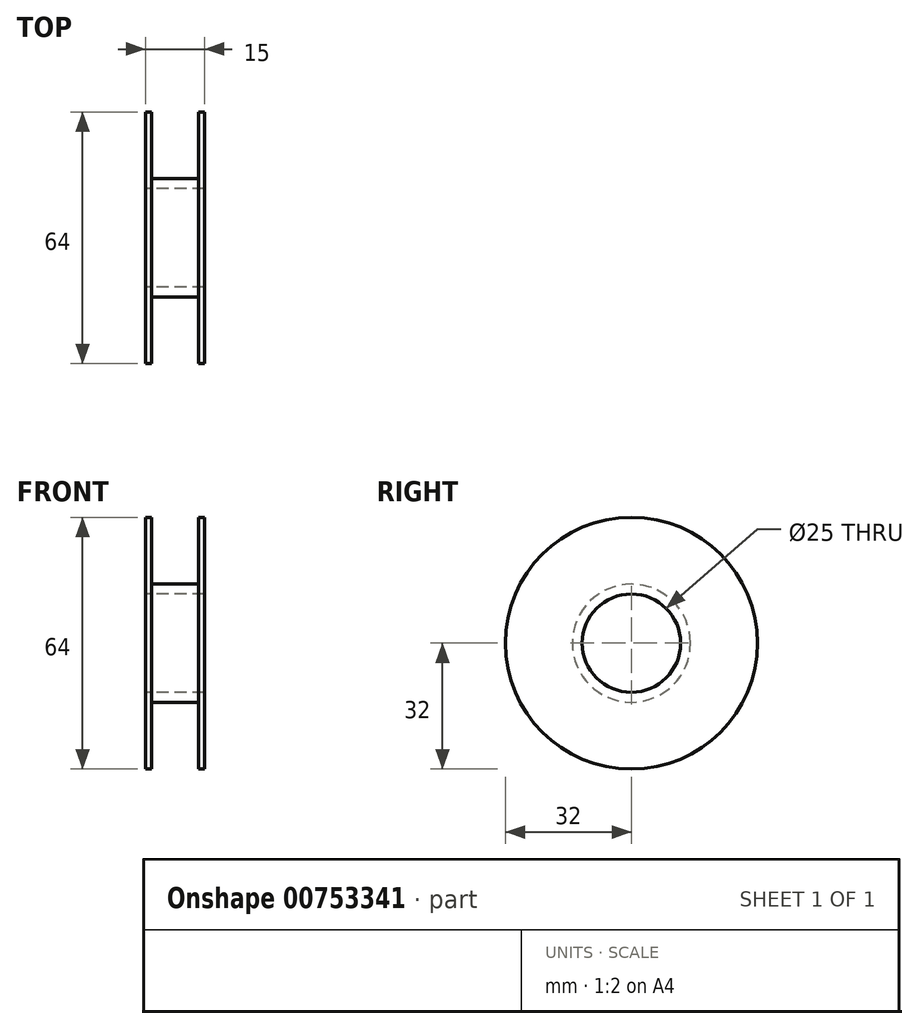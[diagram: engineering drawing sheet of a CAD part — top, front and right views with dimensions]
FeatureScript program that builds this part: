
annotation { "Feature Type Name" : "Feature", "Feature Type Description" : "" }
export const myFeature = defineFeature(function(context is Context, id is Id, definition is map)
    precondition{}
    {
        {
            var Q0;
            Q0=qCreatedBy(makeId("Front.planeOp"),FACE);
            var sketch = newSketch(context, id + "F0", { "sketchPlane" : qUnion([Q0])});
            skLineSegment(sketch, "E0", {"start": v(-7.5, 12.5) * mm, "end": v(-7.5, 32) * mm});
            skLineSegment(sketch, "E1", {"start": v(-7.5, 32) * mm, "end": v(-6, 32) * mm});
            skLineSegment(sketch, "E2", {"start": v(-6, 32) * mm, "end": v(-6, 15) * mm});
            skLineSegment(sketch, "E3", {"start": v(-6, 15) * mm, "end": v(6, 15) * mm});
            skLineSegment(sketch, "E4", {"start": v(6, 15) * mm, "end": v(6, 32) * mm});
            skLineSegment(sketch, "E5", {"start": v(6, 32) * mm, "end": v(7.5, 32) * mm});
            skLineSegment(sketch, "E6", {"start": v(7.5, 32) * mm, "end": v(7.5, 12.5) * mm});
            skLineSegment(sketch, "E7", {"start": v(7.5, 12.5) * mm, "end": v(-7.5, 12.5) * mm});
            skLineSegment(sketch, "E8", {"start": v(-13.31, 0) * mm, "end": v(12.92, 0) * mm, "construction": true});
            skSolve(sketch);
        }
        {
            var Q0;
            Q0 = qSketchRegion(id + "F0", true);
            var Q1;
            Q1=sQuery(id+"F0.wireOp",EDGE,"E8");
            revolve(context, id + "F1", {"surfaceOperationType" : NewSurfaceOperationType.NEW, "entities" : qUnion([Q0]), "axis" : qUnion([Q1]), "revolveType" : RevolveType.FULL});
        }
    });
